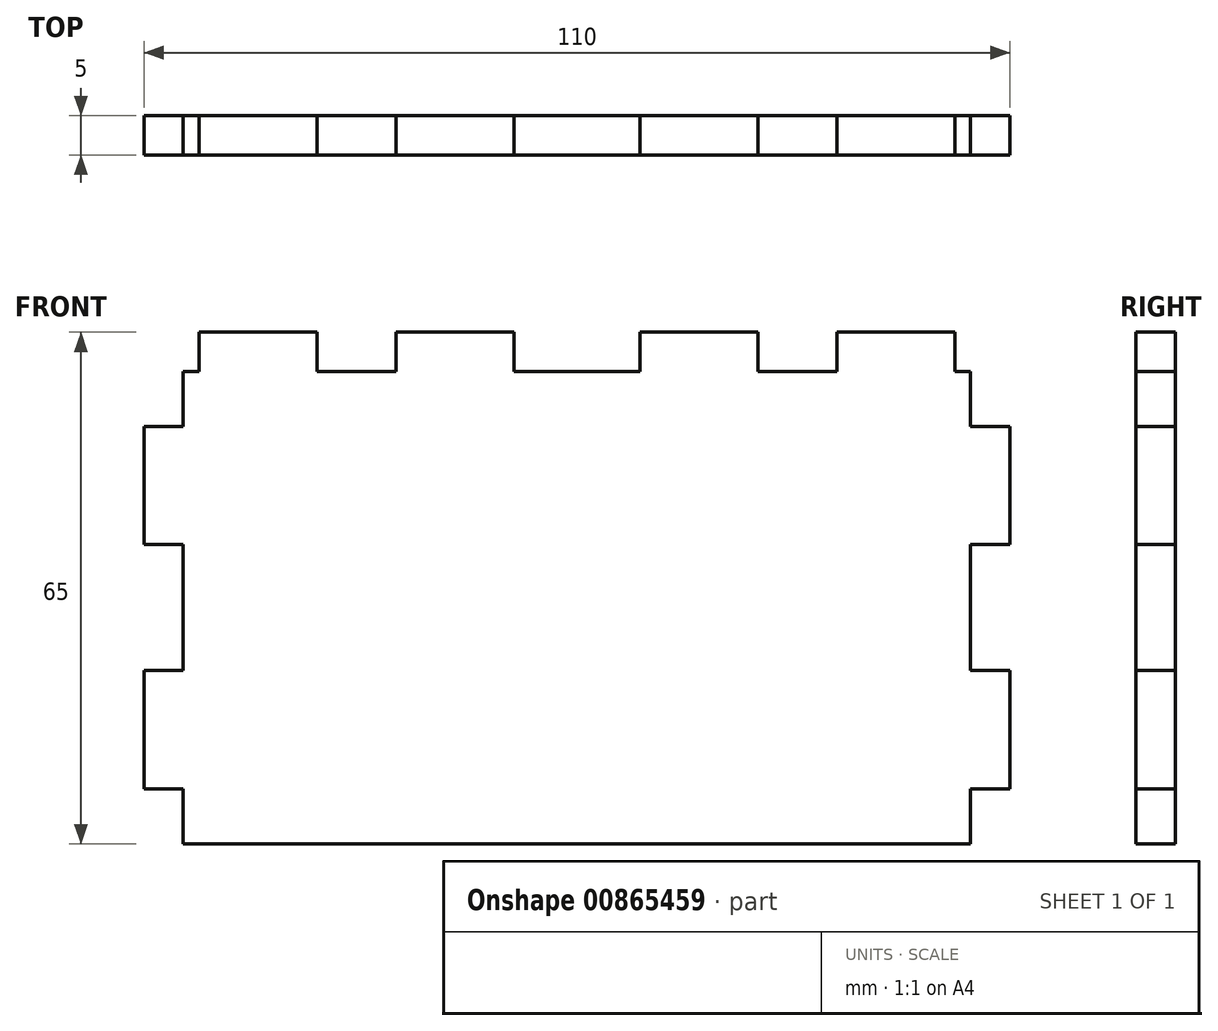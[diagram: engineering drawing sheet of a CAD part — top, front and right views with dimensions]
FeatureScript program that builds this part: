
annotation { "Feature Type Name" : "Feature", "Feature Type Description" : "" }
export const myFeature = defineFeature(function(context is Context, id is Id, definition is map)
    precondition{}
    {
        {
            var Q0;
            Q0=qCreatedBy(makeId("Front.planeOp"),FACE);
            var sketch = newSketch(context, id + "F0", { "sketchPlane" : qUnion([Q0])});
            skLineSegment(sketch, "E0.bottom", {"start": v(50, -30) * mm, "end": v(-50, -30) * mm});
            skLineSegment(sketch, "E0.top", {"start": v(50, 30) * mm, "end": v(48, 30) * mm});
            skLineSegment(sketch, "E0.left", {"start": v(50, -30) * mm, "end": v(50, -23) * mm});
            skLineSegment(sketch, "E0.right", {"start": v(-50, -30) * mm, "end": v(-50, -23) * mm});
            skPoint(sketch, "E0.middle", {"position": v(0, 0) * mm});
            skLineSegment(sketch, "E1", {"start": v(-48, 30) * mm, "end": v(-48, 35) * mm});
            skLineSegment(sketch, "E2", {"start": v(-48, 35) * mm, "end": v(-33, 35) * mm});
            skLineSegment(sketch, "E3", {"start": v(-33, 35) * mm, "end": v(-33, 30) * mm});
            skLineSegment(sketch, "E4", {"start": v(-23, 30) * mm, "end": v(-23, 35) * mm});
            skLineSegment(sketch, "E5", {"start": v(-23, 35) * mm, "end": v(-8, 35) * mm});
            skLineSegment(sketch, "E6", {"start": v(-8, 35) * mm, "end": v(-8, 30) * mm});
            skLineSegment(sketch, "E7.MirrorCS", {"start": v(8, 35) * mm, "end": v(8, 30) * mm});
            skLineSegment(sketch, "E8.MirrorCS", {"start": v(23, 35) * mm, "end": v(8, 35) * mm});
            skLineSegment(sketch, "E9.MirrorCS", {"start": v(23, 30) * mm, "end": v(23, 35) * mm});
            skLineSegment(sketch, "E10.MirrorCS", {"start": v(33, 35) * mm, "end": v(33, 30) * mm});
            skLineSegment(sketch, "E11.MirrorCS", {"start": v(48, 35) * mm, "end": v(33, 35) * mm});
            skLineSegment(sketch, "E12.MirrorCS", {"start": v(48, 30) * mm, "end": v(48, 35) * mm});
            skLineSegment(sketch, "E13.trimOffspring", {"start": v(-48, 30) * mm, "end": v(-50, 30) * mm});
            skLineSegment(sketch, "E14.trimOffspring", {"start": v(-23, 30) * mm, "end": v(-33, 30) * mm});
            skLineSegment(sketch, "E15.trimOffspring", {"start": v(8, 30) * mm, "end": v(-8, 30) * mm});
            skLineSegment(sketch, "E16.trimOffspring", {"start": v(33, 30) * mm, "end": v(23, 30) * mm});
            skPoint(sketch, "E17.middle", {"position": v(-47.89, 15.5) * mm});
            skLineSegment(sketch, "E18", {"start": v(-50, 23) * mm, "end": v(-55, 23) * mm});
            skLineSegment(sketch, "E19", {"start": v(-55, 23) * mm, "end": v(-55, 8) * mm});
            skLineSegment(sketch, "E20", {"start": v(-55, 8) * mm, "end": v(-50, 8) * mm});
            skLineSegment(sketch, "E21.trimOffspring", {"start": v(-50, 23) * mm, "end": v(-50, 30) * mm});
            skLineSegment(sketch, "E22.MirrorCS", {"start": v(50, 23) * mm, "end": v(55, 23) * mm});
            skLineSegment(sketch, "E23.MirrorCS", {"start": v(55, 23) * mm, "end": v(55, 8) * mm});
            skLineSegment(sketch, "E24.MirrorCS", {"start": v(55, 8) * mm, "end": v(50, 8) * mm});
            skLineSegment(sketch, "E25.MirrorCS", {"start": v(-55, -23) * mm, "end": v(-55, -8) * mm});
            skLineSegment(sketch, "E26.MirrorCS", {"start": v(-50, -23) * mm, "end": v(-55, -23) * mm});
            skLineSegment(sketch, "E27.MirrorCS", {"start": v(-55, -8) * mm, "end": v(-50, -8) * mm});
            skLineSegment(sketch, "E28.MirrorCS", {"start": v(50, -23) * mm, "end": v(55, -23) * mm});
            skLineSegment(sketch, "E29.MirrorCS", {"start": v(55, -8) * mm, "end": v(50, -8) * mm});
            skLineSegment(sketch, "E30.MirrorCS", {"start": v(55, -23) * mm, "end": v(55, -8) * mm});
            skLineSegment(sketch, "E31.trimOffspring", {"start": v(-50, -8) * mm, "end": v(-50, 8) * mm});
            skLineSegment(sketch, "E32.trimOffspring", {"start": v(50, 23) * mm, "end": v(50, 30) * mm});
            skLineSegment(sketch, "E33.trimOffspring", {"start": v(50, -8) * mm, "end": v(50, 8) * mm});
            skSolve(sketch);
        }
        {
            var Q0;
            Q0=makeQuery(id+"F0.imprint","IMPRINT",FACE,{"disambiguationData":[TD([[makeQuery(id+"F0.imprint","IMPRINT",EDGE,{"derivedFrom":sQuery(id+"F0.wireOp",EDGE,"E0.bottom")}),-1.0]])]});
            extrude(context, id + "F1", {"entities" : qUnion([Q0]), "depth" : 5 * mm, "offsetDistance" : 25 * mm});
        }
    });
